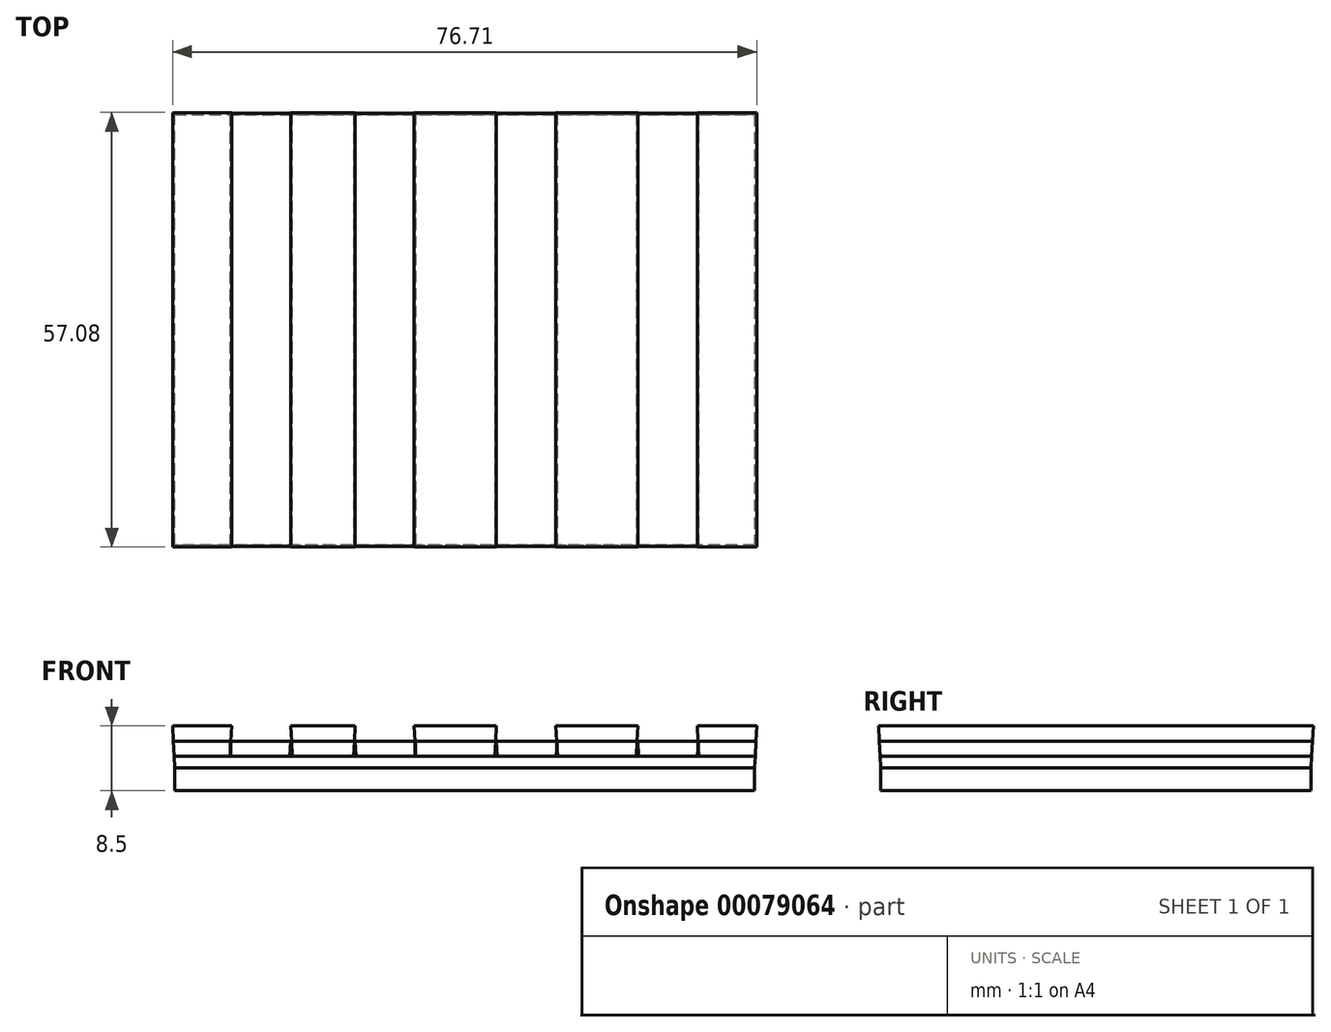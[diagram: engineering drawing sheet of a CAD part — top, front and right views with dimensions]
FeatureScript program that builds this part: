
annotation { "Feature Type Name" : "Feature", "Feature Type Description" : "" }
export const myFeature = defineFeature(function(context is Context, id is Id, definition is map)
    precondition{}
    {
        {
            var Q0;
            Q0=qCreatedBy(makeId("Top.planeOp"),FACE);
            var sketch = newSketch(context, id + "F0", { "sketchPlane" : qUnion([Q0])});
            skLineSegment(sketch, "E0.bottom", {"start": v(-76.14, 56.5) * mm, "end": v(0, 56.5) * mm});
            skLineSegment(sketch, "E0.top", {"start": v(-76.14, 0) * mm, "end": v(0, 0) * mm});
            skLineSegment(sketch, "E0.left", {"start": v(-76.14, 56.5) * mm, "end": v(-76.14, 0) * mm});
            skLineSegment(sketch, "E0.right", {"start": v(0, 56.5) * mm, "end": v(0, 0) * mm});
            skSolve(sketch);
        }
        {
            var Q0;
            Q0=qSketchRegion(id+"F0",true);
            extrude(context, id + "F1", {"entities" : qUnion([Q0]), "depth" : 3 * mm});
        }
        {
            var Q0;
            Q0=makeQuery(id+"F1.opExtrude","CAP_FACE",FACE,{"disambiguationData":[OSD([sQuery(id+"F0.wireOp",EDGE,"E0.bottom"),sQuery(id+"F0.wireOp",EDGE,"E0.top"),sQuery(id+"F0.wireOp",EDGE,"E0.left"),sQuery(id+"F0.wireOp",EDGE,"E0.right")])],"isStart":false});
            var sketch = newSketch(context, id + "F2", { "sketchPlane" : qUnion([Q0])});
            skLineSegment(sketch, "E1.bottom", {"start": v(-76.14, 56.5) * mm, "end": v(0, 56.5) * mm});
            skLineSegment(sketch, "E1.top", {"start": v(-76.14, 0) * mm, "end": v(0, 0) * mm});
            skLineSegment(sketch, "E1.left", {"start": v(-76.14, 56.5) * mm, "end": v(-76.14, 0) * mm});
            skLineSegment(sketch, "E1.right", {"start": v(0, 56.5) * mm, "end": v(0, 0) * mm});
            skSolve(sketch);
        }
        {
            var Q0;
            Q0=makeQuery(id+"F2.imprint","IMPRINT",FACE,{"disambiguationData":[TD([[makeQuery(id+"F2.imprint","IMPRINT",EDGE,{"derivedFrom":sQuery(id+"F2.wireOp",EDGE,"E1.bottom")}),-1.0]])]});
            extrude(context, id + "F3", {"entities" : qUnion([Q0]), "depth" : 1.5 * mm, "hasDraft" : true, "draftAngle" : 3 * degree});
        }
        {
            var Q0;
            Q0=makeQuery(id+"F3.opExtrude","CAP_FACE",FACE,{"disambiguationData":[OSD([sQuery(id+"F2.wireOp",EDGE,"E1.bottom"),sQuery(id+"F2.wireOp",EDGE,"E1.top"),sQuery(id+"F2.wireOp",EDGE,"E1.left"),sQuery(id+"F2.wireOp",EDGE,"E1.right")])],"isStart":false});
            var sketch = newSketch(context, id + "F4", { "sketchPlane" : qUnion([Q0])});
            skLineSegment(sketch, "E2.bottom", {"start": v(-76.22, 56.58) * mm, "end": v(0.08, 56.58) * mm});
            skLineSegment(sketch, "E2.top", {"start": v(-76.22, -0.08) * mm, "end": v(0.08, -0.08) * mm});
            skLineSegment(sketch, "E2.left", {"start": v(-76.22, 56.58) * mm, "end": v(-76.22, -0.08) * mm});
            skLineSegment(sketch, "E2.right", {"start": v(0.08, 56.58) * mm, "end": v(0.08, -0.08) * mm});
            skSolve(sketch);
        }
        {
            var Q0;
            Q0=qSketchRegion(id+"F4",true);
            extrude(context, id + "F5", {"entities" : qUnion([Q0]), "depth" : 2 * mm, "hasDraft" : true, "draftAngle" : 3 * degree});
        }
        {
            var Q0;
            Q0=makeQuery(id+"F5.opExtrude","CAP_FACE",FACE,{"disambiguationData":[OSD([sQuery(id+"F4.wireOp",EDGE,"E2.bottom"),sQuery(id+"F4.wireOp",EDGE,"E2.top"),sQuery(id+"F4.wireOp",EDGE,"E2.left"),sQuery(id+"F4.wireOp",EDGE,"E2.right")])],"isStart":false});
            var sketch = newSketch(context, id + "F6", { "sketchPlane" : qUnion([Q0])});
            skLineSegment(sketch, "E3.bottom", {"start": v(-68.76, 56.68) * mm, "end": v(-60.82, 56.68) * mm});
            skLineSegment(sketch, "E3.top", {"start": v(-68.76, -0.18) * mm, "end": v(-60.82, -0.18) * mm});
            skLineSegment(sketch, "E3.left", {"start": v(-68.76, 56.68) * mm, "end": v(-68.76, -0.18) * mm});
            skLineSegment(sketch, "E3.right", {"start": v(-60.82, 56.68) * mm, "end": v(-60.82, -0.18) * mm});
            skSolve(sketch);
        }
        {
            var Q0;
            Q0=qSketchRegion(id+"F6",true);
            extrude(context, id + "F7", {"entities" : qUnion([Q0]), "operationType" : NewBodyOperationType.REMOVE, "oppositeDirection" : true, "depth" : 2 * mm, "hasDraft" : true, "draftAngle" : 3 * degree});
        }
        {
            var Q0;
            {var subQ0=sQuery(id+"F4.wireOp",EDGE,"E2.bottom");var subQ1=sQuery(id+"F4.wireOp",EDGE,"E2.top");var subQ2=sQuery(id+"F4.wireOp",EDGE,"E2.right");Q0=makeQuery(id+"F7.boolean.opBoolean","SPLIT",FACE,{"disambiguationData":[TD([makeQuery(id+"F5.opExtrude","SWEPT_FACE",FACE,{"disambiguationData":[OSD([subQ2])]})])],"derivedFrom":makeQuery(id+"F5.opExtrude","CAP_FACE",FACE,{"disambiguationData":[OSD([subQ0,subQ1,sQuery(id+"F4.wireOp",EDGE,"E2.left"),subQ2])],"isStart":false})});}
            var sketch = newSketch(context, id + "F8", { "sketchPlane" : qUnion([Q0])});
            skLineSegment(sketch, "E4.bottom", {"start": v(-52.56, 56.68) * mm, "end": v(-44.62, 56.68) * mm});
            skLineSegment(sketch, "E4.top", {"start": v(-52.56, -0.18) * mm, "end": v(-44.62, -0.18) * mm});
            skLineSegment(sketch, "E4.left", {"start": v(-52.56, 56.68) * mm, "end": v(-52.56, -0.18) * mm});
            skLineSegment(sketch, "E4.right", {"start": v(-44.62, 56.68) * mm, "end": v(-44.62, -0.18) * mm});
            skSolve(sketch);
        }
        {
            var Q0;
            Q0=qSketchRegion(id+"F8",true);
            extrude(context, id + "F9", {"entities" : qUnion([Q0]), "operationType" : NewBodyOperationType.REMOVE, "oppositeDirection" : true, "depth" : 2 * mm, "hasDraft" : true, "draftAngle" : 3 * degree});
        }
        {
            var Q0;
            {var subQ0=sQuery(id+"F4.wireOp",EDGE,"E2.bottom");var subQ2=sQuery(id+"F4.wireOp",EDGE,"E2.top");var subQ4=sQuery(id+"F4.wireOp",EDGE,"E2.right");var subQ5=makeQuery(id+"F5.opExtrude","SWEPT_FACE",FACE,{"disambiguationData":[OSD([subQ4])]});Q0=makeQuery(id+"F9.boolean.opBoolean","SPLIT",FACE,{"disambiguationData":[TD([subQ5])],"derivedFrom":makeQuery(id+"F7.boolean.opBoolean","SPLIT",FACE,{"disambiguationData":[TD([subQ5])],"derivedFrom":makeQuery(id+"F5.opExtrude","CAP_FACE",FACE,{"disambiguationData":[OSD([subQ0,subQ2,sQuery(id+"F4.wireOp",EDGE,"E2.left"),subQ4])],"isStart":false})})});}
            var sketch = newSketch(context, id + "F10", { "sketchPlane" : qUnion([Q0])});
            skLineSegment(sketch, "E5.bottom", {"start": v(-34, 56.68) * mm, "end": v(-25.99, 56.68) * mm});
            skLineSegment(sketch, "E5.top", {"start": v(-34, -0.18) * mm, "end": v(-25.99, -0.18) * mm});
            skLineSegment(sketch, "E5.left", {"start": v(-34, 56.68) * mm, "end": v(-34, -0.18) * mm});
            skLineSegment(sketch, "E5.right", {"start": v(-25.99, 56.68) * mm, "end": v(-25.99, -0.18) * mm});
            skSolve(sketch);
        }
        {
            var Q0;
            Q0=qSketchRegion(id+"F10",true);
            extrude(context, id + "F11", {"entities" : qUnion([Q0]), "operationType" : NewBodyOperationType.REMOVE, "oppositeDirection" : true, "depth" : 2 * mm, "hasDraft" : true, "draftAngle" : 3 * degree});
        }
        {
            var Q0;
            {var subQ0=sQuery(id+"F4.wireOp",EDGE,"E2.bottom");var subQ2=sQuery(id+"F4.wireOp",EDGE,"E2.top");var subQ4=sQuery(id+"F4.wireOp",EDGE,"E2.right");var subQ5=makeQuery(id+"F5.opExtrude","SWEPT_FACE",FACE,{"disambiguationData":[OSD([subQ4])]});Q0=makeQuery(id+"F11.boolean.opBoolean","SPLIT",FACE,{"disambiguationData":[TD([subQ5])],"derivedFrom":makeQuery(id+"F9.boolean.opBoolean","SPLIT",FACE,{"disambiguationData":[TD([subQ5])],"derivedFrom":makeQuery(id+"F7.boolean.opBoolean","SPLIT",FACE,{"disambiguationData":[TD([subQ5])],"derivedFrom":makeQuery(id+"F5.opExtrude","CAP_FACE",FACE,{"disambiguationData":[OSD([subQ0,subQ2,sQuery(id+"F4.wireOp",EDGE,"E2.left"),subQ4])],"isStart":false})})})});}
            var sketch = newSketch(context, id + "F12", { "sketchPlane" : qUnion([Q0])});
            skLineSegment(sketch, "E6.bottom", {"start": v(-15.44, 56.68) * mm, "end": v(-7.42, 56.68) * mm});
            skLineSegment(sketch, "E6.top", {"start": v(-15.44, -0.18) * mm, "end": v(-7.42, -0.18) * mm});
            skLineSegment(sketch, "E6.left", {"start": v(-15.44, 56.68) * mm, "end": v(-15.44, -0.18) * mm});
            skLineSegment(sketch, "E6.right", {"start": v(-7.42, 56.68) * mm, "end": v(-7.42, -0.18) * mm});
            skSolve(sketch);
        }
        {
            var Q0;
            Q0=qSketchRegion(id+"F12",true);
            extrude(context, id + "F13", {"entities" : qUnion([Q0]), "operationType" : NewBodyOperationType.REMOVE, "oppositeDirection" : true, "depth" : 2 * mm, "hasDraft" : true, "draftAngle" : 3 * degree});
        }
        {
            var Q0;
            {var subQ0=sQuery(id+"F4.wireOp",EDGE,"E2.bottom");var subQ1=sQuery(id+"F4.wireOp",EDGE,"E2.top");var subQ2=sQuery(id+"F4.wireOp",EDGE,"E2.left");Q0=makeQuery(id+"F7.boolean.opBoolean","SPLIT",FACE,{"disambiguationData":[TD([makeQuery(id+"F5.opExtrude","SWEPT_FACE",FACE,{"disambiguationData":[OSD([subQ2])]})])],"derivedFrom":makeQuery(id+"F5.opExtrude","CAP_FACE",FACE,{"disambiguationData":[OSD([subQ0,subQ1,subQ2,sQuery(id+"F4.wireOp",EDGE,"E2.right")])],"isStart":false})});}
            var sketch = newSketch(context, id + "F14", { "sketchPlane" : qUnion([Q0])});
            skLineSegment(sketch, "E7.bottom", {"start": v(-76.32, 56.68) * mm, "end": v(-68.76, 56.68) * mm});
            skLineSegment(sketch, "E7.top", {"start": v(-76.32, -0.18) * mm, "end": v(-68.76, -0.18) * mm});
            skLineSegment(sketch, "E7.left", {"start": v(-76.32, 56.68) * mm, "end": v(-76.32, -0.18) * mm});
            skLineSegment(sketch, "E7.right", {"start": v(-68.76, 56.68) * mm, "end": v(-68.76, -0.18) * mm});
            skSolve(sketch);
        }
        {
            var Q0;
            Q0 = qSketchRegion(id + "F14", true);
            extrude(context, id + "F15", {"entities" : qUnion([Q0]), "depth" : 2 * mm, "hasDraft" : true, "draftAngle" : 3 * degree});
        }
        {
            var Q0;
            {var subQ0=sQuery(id+"F4.wireOp",EDGE,"E2.bottom");var subQ2=sQuery(id+"F4.wireOp",EDGE,"E2.top");var subQ4=makeQuery(id+"F7.opExtrude","SWEPT_FACE",FACE,{"disambiguationData":[OSD([sQuery(id+"F6.wireOp",EDGE,"E3.right")])]});var subQ5=sQuery(id+"F4.wireOp",EDGE,"E2.right");Q0=makeQuery(id+"F9.boolean.opBoolean","SPLIT",FACE,{"disambiguationData":[TD([makeQuery(id+"F7.boolean.opBoolean","COPY",FACE,{"derivedFrom":subQ4})])],"derivedFrom":makeQuery(id+"F7.boolean.opBoolean","SPLIT",FACE,{"disambiguationData":[TD([makeQuery(id+"F5.opExtrude","SWEPT_FACE",FACE,{"disambiguationData":[OSD([subQ5])]})])],"derivedFrom":makeQuery(id+"F5.opExtrude","CAP_FACE",FACE,{"disambiguationData":[OSD([subQ0,subQ2,sQuery(id+"F4.wireOp",EDGE,"E2.left"),subQ5])],"isStart":false})})});}
            var sketch = newSketch(context, id + "F16", { "sketchPlane" : qUnion([Q0])});
            skLineSegment(sketch, "E8.bottom", {"start": v(-60.82, 56.68) * mm, "end": v(-52.56, 56.68) * mm});
            skLineSegment(sketch, "E8.top", {"start": v(-60.82, -0.18) * mm, "end": v(-52.56, -0.18) * mm});
            skLineSegment(sketch, "E8.left", {"start": v(-60.82, 56.68) * mm, "end": v(-60.82, -0.18) * mm});
            skLineSegment(sketch, "E8.right", {"start": v(-52.56, 56.68) * mm, "end": v(-52.56, -0.18) * mm});
            skSolve(sketch);
        }
        {
            var Q0;
            Q0 = qSketchRegion(id + "F16", true);
            extrude(context, id + "F17", {"entities" : qUnion([Q0]), "depth" : 2 * mm, "hasDraft" : true, "draftAngle" : 3 * degree});
        }
        {
            var Q0;
            Q0=makeQuery(id+"F3.opExtrude","CAP_FACE",FACE,{"disambiguationData":[OSD([sQuery(id+"F2.wireOp",EDGE,"E1.bottom"),sQuery(id+"F2.wireOp",EDGE,"E1.top"),sQuery(id+"F2.wireOp",EDGE,"E1.left"),sQuery(id+"F2.wireOp",EDGE,"E1.right")])],"isStart":false});
            var sketch = newSketch(context, id + "F18", { "sketchPlane" : qUnion([Q0])});
            skLineSegment(sketch, "E9.bottom", {"start": v(-68.78, 56.58) * mm, "end": v(-61.04, 56.58) * mm});
            skLineSegment(sketch, "E9.top", {"start": v(-68.78, -0.08) * mm, "end": v(-61.04, -0.08) * mm});
            skLineSegment(sketch, "E9.left", {"start": v(-68.78, 56.58) * mm, "end": v(-68.78, -0.08) * mm});
            skLineSegment(sketch, "E9.right", {"start": v(-61.04, 56.58) * mm, "end": v(-61.04, -0.08) * mm});
            skSolve(sketch);
        }
        {
            var Q0;
            Q0 = qSketchRegion(id + "F18", true);
            extrude(context, id + "F19", {"entities" : qUnion([Q0]), "depth" : 2 * mm, "hasDraft" : true, "draftAngle" : 3 * degree});
        }
        {
            var Q0;
            Q0=makeQuery(id+"F3.opExtrude","CAP_FACE",FACE,{"disambiguationData":[OSD([sQuery(id+"F2.wireOp",EDGE,"E1.bottom"),sQuery(id+"F2.wireOp",EDGE,"E1.top"),sQuery(id+"F2.wireOp",EDGE,"E1.left"),sQuery(id+"F2.wireOp",EDGE,"E1.right")])],"isStart":false});
            var sketch = newSketch(context, id + "F20", { "sketchPlane" : qUnion([Q0])});
            skLineSegment(sketch, "E10.bottom", {"start": v(-52.37, 56.58) * mm, "end": v(-44.62, 56.58) * mm});
            skLineSegment(sketch, "E10.top", {"start": v(-52.37, -0.08) * mm, "end": v(-44.62, -0.08) * mm});
            skLineSegment(sketch, "E10.left", {"start": v(-52.37, 56.58) * mm, "end": v(-52.37, -0.08) * mm});
            skLineSegment(sketch, "E10.right", {"start": v(-44.62, 56.58) * mm, "end": v(-44.62, -0.08) * mm});
            skSolve(sketch);
        }
        {
            var Q0;
            Q0 = qSketchRegion(id + "F20", true);
            extrude(context, id + "F21", {"entities" : qUnion([Q0]), "depth" : 2 * mm, "hasDraft" : true, "draftAngle" : 3 * degree});
        }
        {
            var Q0;
            {var subQ0=sQuery(id+"F4.wireOp",EDGE,"E2.bottom");var subQ2=sQuery(id+"F4.wireOp",EDGE,"E2.top");var subQ4=makeQuery(id+"F9.opExtrude","SWEPT_FACE",FACE,{"disambiguationData":[OSD([sQuery(id+"F8.wireOp",EDGE,"E4.right")])]});var subQ5=sQuery(id+"F4.wireOp",EDGE,"E2.right");var subQ6=makeQuery(id+"F5.opExtrude","SWEPT_FACE",FACE,{"disambiguationData":[OSD([subQ5])]});Q0=makeQuery(id+"F11.boolean.opBoolean","SPLIT",FACE,{"disambiguationData":[TD([makeQuery(id+"F9.boolean.opBoolean","COPY",FACE,{"derivedFrom":subQ4})])],"derivedFrom":makeQuery(id+"F9.boolean.opBoolean","SPLIT",FACE,{"disambiguationData":[TD([subQ6])],"derivedFrom":makeQuery(id+"F7.boolean.opBoolean","SPLIT",FACE,{"disambiguationData":[TD([subQ6])],"derivedFrom":makeQuery(id+"F5.opExtrude","CAP_FACE",FACE,{"disambiguationData":[OSD([subQ0,subQ2,sQuery(id+"F4.wireOp",EDGE,"E2.left"),subQ5])],"isStart":false})})})});}
            var sketch = newSketch(context, id + "F22", { "sketchPlane" : qUnion([Q0])});
            skLineSegment(sketch, "E11.bottom", {"start": v(-44.62, 56.68) * mm, "end": v(-34, 56.68) * mm});
            skLineSegment(sketch, "E11.top", {"start": v(-44.62, -0.18) * mm, "end": v(-34, -0.18) * mm});
            skLineSegment(sketch, "E11.left", {"start": v(-44.62, 56.68) * mm, "end": v(-44.62, -0.18) * mm});
            skLineSegment(sketch, "E11.right", {"start": v(-34, 56.68) * mm, "end": v(-34, -0.18) * mm});
            skSolve(sketch);
        }
        {
            var Q0;
            Q0 = qSketchRegion(id + "F22", true);
            extrude(context, id + "F23", {"entities" : qUnion([Q0]), "depth" : 2 * mm, "hasDraft" : true, "draftAngle" : 3 * degree});
        }
        {
            var Q0;
            Q0=makeQuery(id+"F3.opExtrude","CAP_FACE",FACE,{"disambiguationData":[OSD([sQuery(id+"F2.wireOp",EDGE,"E1.bottom"),sQuery(id+"F2.wireOp",EDGE,"E1.top"),sQuery(id+"F2.wireOp",EDGE,"E1.left"),sQuery(id+"F2.wireOp",EDGE,"E1.right")])],"isStart":false});
            var sketch = newSketch(context, id + "F24", { "sketchPlane" : qUnion([Q0])});
            skLineSegment(sketch, "E12.bottom", {"start": v(-33.8, 56.58) * mm, "end": v(-26.06, 56.58) * mm});
            skLineSegment(sketch, "E12.top", {"start": v(-33.8, -0.08) * mm, "end": v(-26.06, -0.08) * mm});
            skLineSegment(sketch, "E12.left", {"start": v(-33.8, 56.58) * mm, "end": v(-33.8, -0.08) * mm});
            skLineSegment(sketch, "E12.right", {"start": v(-26.06, 56.58) * mm, "end": v(-26.06, -0.08) * mm});
            skSolve(sketch);
        }
        {
            var Q0;
            Q0 = qSketchRegion(id + "F24", true);
            extrude(context, id + "F25", {"entities" : qUnion([Q0]), "depth" : 2 * mm, "hasDraft" : true, "draftAngle" : 3 * degree});
        }
        {
            var Q0;
            {var subQ0=sQuery(id+"F4.wireOp",EDGE,"E2.bottom");var subQ2=sQuery(id+"F4.wireOp",EDGE,"E2.top");var subQ4=makeQuery(id+"F11.opExtrude","SWEPT_FACE",FACE,{"disambiguationData":[OSD([sQuery(id+"F10.wireOp",EDGE,"E5.right")])]});var subQ5=sQuery(id+"F4.wireOp",EDGE,"E2.right");var subQ6=makeQuery(id+"F5.opExtrude","SWEPT_FACE",FACE,{"disambiguationData":[OSD([subQ5])]});Q0=makeQuery(id+"F13.boolean.opBoolean","SPLIT",FACE,{"disambiguationData":[TD([makeQuery(id+"F11.boolean.opBoolean","COPY",FACE,{"derivedFrom":subQ4})])],"derivedFrom":makeQuery(id+"F11.boolean.opBoolean","SPLIT",FACE,{"disambiguationData":[TD([subQ6])],"derivedFrom":makeQuery(id+"F9.boolean.opBoolean","SPLIT",FACE,{"disambiguationData":[TD([subQ6])],"derivedFrom":makeQuery(id+"F7.boolean.opBoolean","SPLIT",FACE,{"disambiguationData":[TD([subQ6])],"derivedFrom":makeQuery(id+"F5.opExtrude","CAP_FACE",FACE,{"disambiguationData":[OSD([subQ0,subQ2,sQuery(id+"F4.wireOp",EDGE,"E2.left"),subQ5])],"isStart":false})})})})});}
            var sketch = newSketch(context, id + "F26", { "sketchPlane" : qUnion([Q0])});
            skLineSegment(sketch, "E13.bottom", {"start": v(-25.99, 56.68) * mm, "end": v(-15.44, 56.68) * mm});
            skLineSegment(sketch, "E13.top", {"start": v(-25.99, -0.18) * mm, "end": v(-15.44, -0.18) * mm});
            skLineSegment(sketch, "E13.left", {"start": v(-25.99, 56.68) * mm, "end": v(-25.99, -0.18) * mm});
            skLineSegment(sketch, "E13.right", {"start": v(-15.44, 56.68) * mm, "end": v(-15.44, -0.18) * mm});
            skSolve(sketch);
        }
        {
            var Q0;
            Q0 = qSketchRegion(id + "F26", true);
            extrude(context, id + "F27", {"entities" : qUnion([Q0]), "depth" : 2 * mm, "hasDraft" : true, "draftAngle" : 3 * degree});
        }
        {
            var Q0;
            Q0=makeQuery(id+"F3.opExtrude","CAP_FACE",FACE,{"disambiguationData":[OSD([sQuery(id+"F2.wireOp",EDGE,"E1.bottom"),sQuery(id+"F2.wireOp",EDGE,"E1.top"),sQuery(id+"F2.wireOp",EDGE,"E1.left"),sQuery(id+"F2.wireOp",EDGE,"E1.right")])],"isStart":false});
            var sketch = newSketch(context, id + "F28", { "sketchPlane" : qUnion([Q0])});
            skLineSegment(sketch, "E14.bottom", {"start": v(-15.24, 56.58) * mm, "end": v(-7.49, 56.58) * mm});
            skLineSegment(sketch, "E14.top", {"start": v(-15.24, -0.08) * mm, "end": v(-7.49, -0.08) * mm});
            skLineSegment(sketch, "E14.left", {"start": v(-15.24, 56.58) * mm, "end": v(-15.24, -0.08) * mm});
            skLineSegment(sketch, "E14.right", {"start": v(-7.49, 56.58) * mm, "end": v(-7.49, -0.08) * mm});
            skSolve(sketch);
        }
        {
            var Q0;
            Q0 = qSketchRegion(id + "F28", true);
            extrude(context, id + "F29", {"entities" : qUnion([Q0]), "depth" : 2 * mm, "hasDraft" : true, "draftAngle" : 3 * degree});
        }
        {
            var Q0;
            {var subQ0=sQuery(id+"F4.wireOp",EDGE,"E2.bottom");var subQ2=sQuery(id+"F4.wireOp",EDGE,"E2.top");var subQ4=sQuery(id+"F4.wireOp",EDGE,"E2.right");var subQ5=makeQuery(id+"F5.opExtrude","SWEPT_FACE",FACE,{"disambiguationData":[OSD([subQ4])]});Q0=makeQuery(id+"F13.boolean.opBoolean","SPLIT",FACE,{"disambiguationData":[TD([subQ5])],"derivedFrom":makeQuery(id+"F11.boolean.opBoolean","SPLIT",FACE,{"disambiguationData":[TD([subQ5])],"derivedFrom":makeQuery(id+"F9.boolean.opBoolean","SPLIT",FACE,{"disambiguationData":[TD([subQ5])],"derivedFrom":makeQuery(id+"F7.boolean.opBoolean","SPLIT",FACE,{"disambiguationData":[TD([subQ5])],"derivedFrom":makeQuery(id+"F5.opExtrude","CAP_FACE",FACE,{"disambiguationData":[OSD([subQ0,subQ2,sQuery(id+"F4.wireOp",EDGE,"E2.left"),subQ4])],"isStart":false})})})})});}
            var sketch = newSketch(context, id + "F30", { "sketchPlane" : qUnion([Q0])});
            skLineSegment(sketch, "E15.bottom", {"start": v(-7.42, 56.68) * mm, "end": v(0.18, 56.68) * mm});
            skLineSegment(sketch, "E15.top", {"start": v(-7.42, -0.18) * mm, "end": v(0.18, -0.18) * mm});
            skLineSegment(sketch, "E15.left", {"start": v(-7.42, 56.68) * mm, "end": v(-7.42, -0.18) * mm});
            skLineSegment(sketch, "E15.right", {"start": v(0.18, 56.68) * mm, "end": v(0.18, -0.18) * mm});
            skSolve(sketch);
        }
        {
            var Q0;
            Q0 = qSketchRegion(id + "F30", true);
            extrude(context, id + "F31", {"entities" : qUnion([Q0]), "depth" : 2 * mm, "hasDraft" : true, "draftAngle" : 3 * degree});
        }
    });
